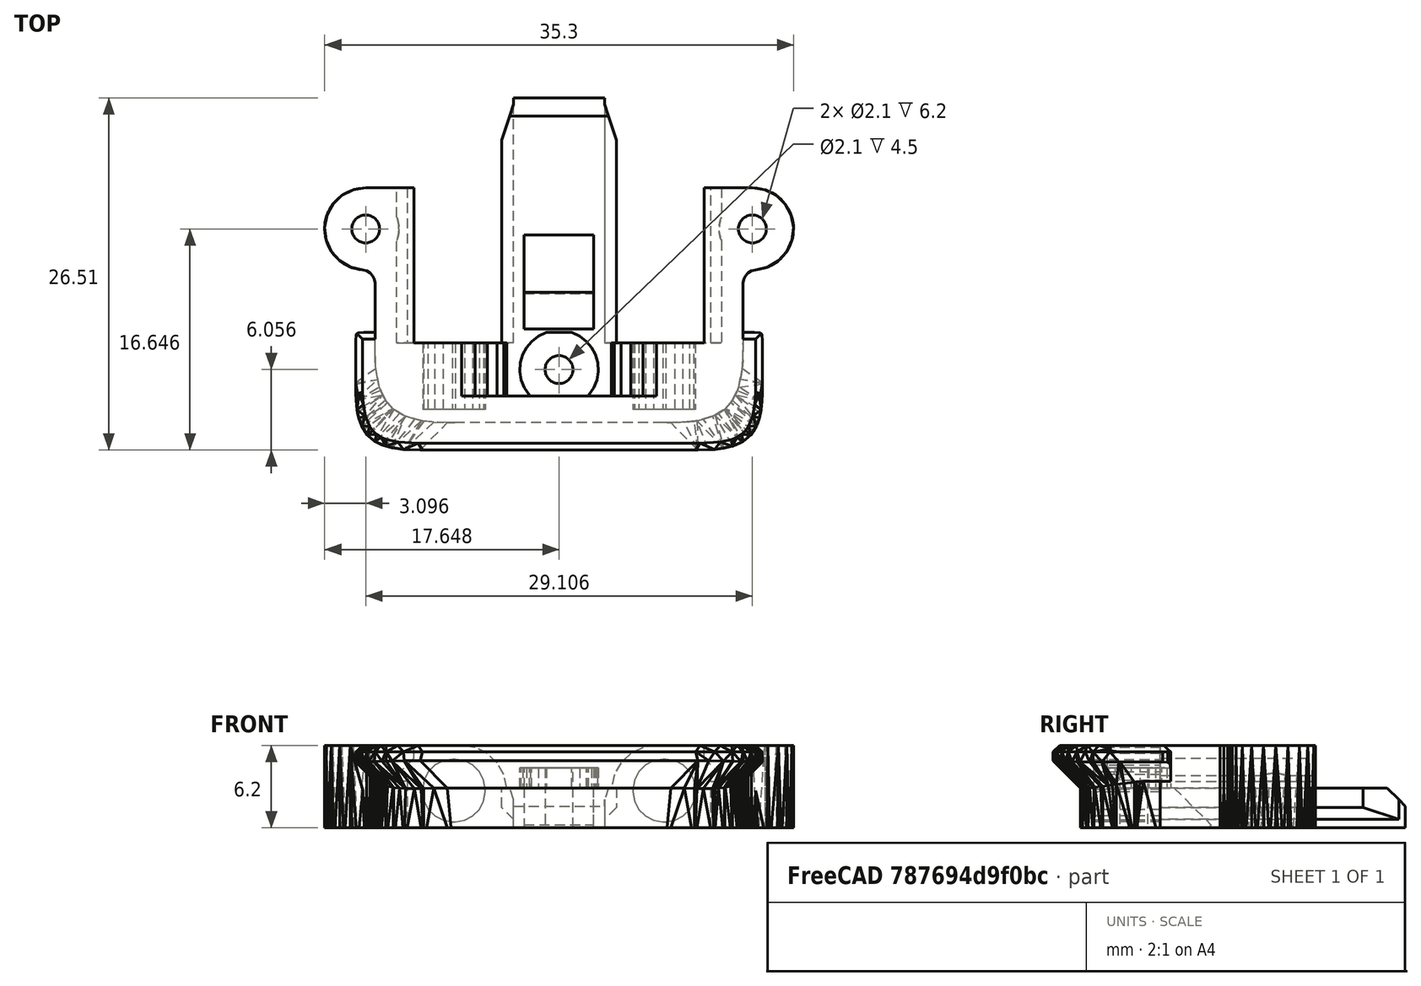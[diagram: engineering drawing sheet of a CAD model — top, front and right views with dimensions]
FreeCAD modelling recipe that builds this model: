
FCSTD DOCUMENT  (FreeCAD 0.20R29177 +426 (Git))
Label: deckmate_bottom_no_insert
License: All rights reserved
LicenseURL: http://en.wikipedia.org/wiki/All_rights_reserved
objects: Sketcher::SketchObject×3, Part::Feature×2, PartDesign::Pad×2, Mesh::Feature×1, Part::Refine×1, PartDesign::FeatureBase×1, PartDesign::Pocket×1, PartDesign::Body×1
note: 14 computed .brp shape members not serialized (recipe doc carries the construction recipe); baked Part::Feature solids carry a one-line shape summary decoded from their .brp

FEATURE [Mesh::Feature] Deck_Mate_Mechanism_Bot_Print_02
FEATURE [Part::Feature] Deck_Mate_Mechanism_Bot_Print_02001
  shape: bbox 35.3 x 26.5 x 7.7 mm, 1562 faces, 0 solids (baked)
FEATURE [Part::Feature] Deck_Mate_Mechanism_Bot_Print_02001_solid  label="Deck_Mate_Mechanism_Bot_Print_02001 (Solid)"
  shape: bbox 35.3 x 26.5 x 7.7 mm, 1562 faces (baked)
FEATURE [Part::Refine] Deck_Mate_Mechanism_Bot_Print_02001_solid001  label="Deck_Mate_Mechanism_Bot_Print_02001 (Solid)001"
  Source = -> Deck_Mate_Mechanism_Bot_Print_02001_solid
FEATURE [PartDesign::FeatureBase] BaseFeature
  BaseFeature = -> Deck_Mate_Mechanism_Bot_Print_02001_solid001
FEATURE [Sketcher::SketchObject] Sketch
  ExternalGeometry = -> [BaseFeature]
  FullyConstrained = true
  MapMode = 5
  Placement = pos=(0,0,-26.6092) rot=(1,0,0;3.14159rad)
  Support = -> [BaseFeature]
  sketch-geometry (6):
    g0: Circle CenterX=50.636 CenterY=-198.486 CenterZ=0 NormalX=0 NormalY=0 NormalZ=1 AngleXU=0 Radius=1.20441
    g1: Circle CenterX=79.742 CenterY=-198.486 CenterZ=0 NormalX=0 NormalY=0 NormalZ=1 AngleXU=0 Radius=1.20439
    g2: Circle CenterX=50.636 CenterY=-198.486 CenterZ=0 NormalX=0 NormalY=0 NormalZ=1 AngleXU=0 Radius=2.5
    g3: Circle CenterX=79.742 CenterY=-198.486 CenterZ=0 NormalX=0 NormalY=0 NormalZ=1 AngleXU=0 Radius=2.5
    g4: Circle CenterX=50.636 CenterY=-198.486 CenterZ=0 NormalX=0 NormalY=0 NormalZ=1 AngleXU=0 Radius=1.05
    g5: Circle CenterX=79.742 CenterY=-198.486 CenterZ=0 NormalX=0 NormalY=0 NormalZ=1 AngleXU=0 Radius=1.05
  constraints (14):
    c: PointOnObject(g-3,g0)
    c: PointOnObject(g-4,g0)
    c: PointOnObject(g-5,g0)
    c: PointOnObject(g-6,g1)
    c: PointOnObject(g-7,g1)
    c: PointOnObject(g-8,g1)
    c: Coincident(g2,g0)
    c: Coincident(g3,g1)
    c: Diameter(g2) = 5
    c: Coincident(g4,g2)
    c: Coincident(g5,g3)
    c: Diameter(g4) = 2.1
    c: Equal(g2,g3)
    c: Equal(g4,g5)
FEATURE [PartDesign::Pad] Pad
  BaseFeature = -> BaseFeature
  Direction = (0,0,-1)
  Length = 10
  Length2 = 10
  Profile = -> Sketch
  ReferenceAxis = -> Sketch [N_Axis]
  Reversed = true
  Type = 3
  UpToFace = -> BaseFeature [Face781]
FEATURE [Sketcher::SketchObject] Sketch001
  ExternalGeometry = -> [Pad]
  FullyConstrained = true
  MapMode = 5
  Placement = pos=(0,0,-26.6092) rot=(1,0,0;3.14159rad)
  Support = -> [Pad]
  sketch-geometry (3):
    g0: Circle CenterX=65.1884 CenterY=-187.896 CenterZ=0 NormalX=0 NormalY=0 NormalZ=1 AngleXU=0 Radius=2.28576
    g1: Circle CenterX=65.1884 CenterY=-187.896 CenterZ=0 NormalX=0 NormalY=0 NormalZ=1 AngleXU=0 Radius=2.5
    g2: Circle CenterX=65.1884 CenterY=-187.896 CenterZ=0 NormalX=0 NormalY=0 NormalZ=1 AngleXU=0 Radius=1.05
  constraints (7):
    c: PointOnObject(g-3,g0)
    c: PointOnObject(g-4,g0)
    c: PointOnObject(g-5,g0)
    c: Coincident(g1,g0)
    c: Coincident(g2,g1)
    c: Diameter(g1) = 5
    c: Diameter(g2) = 2.1
FEATURE [PartDesign::Pad] Pad001
  BaseFeature = -> Pad
  Direction = (0,0,-1)
  Length = 10
  Length2 = 10
  Profile = -> Sketch001
  ReferenceAxis = -> Sketch001 [N_Axis]
  Type = 3
  UpToFace = -> Pad [Face88]
FEATURE [Sketcher::SketchObject] Sketch003
  ExternalGeometry = -> [Pad001]
  FullyConstrained = true
  MapMode = 5
  Placement = pos=(0,0,-26.6092) rot=(1,0,0;3.14159rad)
  Support = -> [Pad001]
  sketch-geometry (6):
    g0: Circle CenterX=50.636 CenterY=-198.486 CenterZ=0 NormalX=0 NormalY=0 NormalZ=1 AngleXU=0 Radius=5
    g1: Circle CenterX=79.742 CenterY=-198.486 CenterZ=0 NormalX=0 NormalY=0 NormalZ=1 AngleXU=0 Radius=5
    g2: LineSegment StartX=45.636 StartY=-180.844 StartZ=0 EndX=84.742 EndY=-180.844 EndZ=0
    g3: LineSegment StartX=84.742 StartY=-180.844 StartZ=0 EndX=84.742 EndY=-209.346 EndZ=0
    g4: LineSegment StartX=84.742 StartY=-209.346 StartZ=0 EndX=45.636 EndY=-209.346 EndZ=0
    g5: LineSegment StartX=45.636 StartY=-209.346 StartZ=0 EndX=45.636 EndY=-180.844 EndZ=0
  constraints (16):
    c: Coincident(g0,g-5)
    c: Coincident(g1,g-6)
    c: Equal(g0,g1)
    c: Diameter(g0) = 10
    c: Coincident(g2,g3)
    c: Coincident(g3,g4)
    c: Coincident(g4,g5)
    c: Coincident(g5,g2)
    c: Horizontal(g2)
    c: Horizontal(g4)
    c: Vertical(g3)
    c: Vertical(g5)
    c: Tangent(g3,g1)
    c: Tangent(g0,g5)
    c: DistanceY(g3,g-3) = 1
    c: DistanceY(g-4,g2) = 1
FEATURE [PartDesign::Pocket] Pocket
  BaseFeature = -> Pad001
  Direction = (0,0,1)
  Length = 1.5
  Length2 = 5
  Profile = -> Sketch003
  ReferenceAxis = -> Sketch003 [N_Axis]
  Type = 0
FEATURE [PartDesign::Body] Body
  BaseFeature = -> Deck_Mate_Mechanism_Bot_Print_02001_solid001
  Group = -> [BaseFeature,Sketch,Pad,Sketch001,Pad001,Sketch003,Pocket]
  Origin = -> Origin
  Tip = -> Pocket
